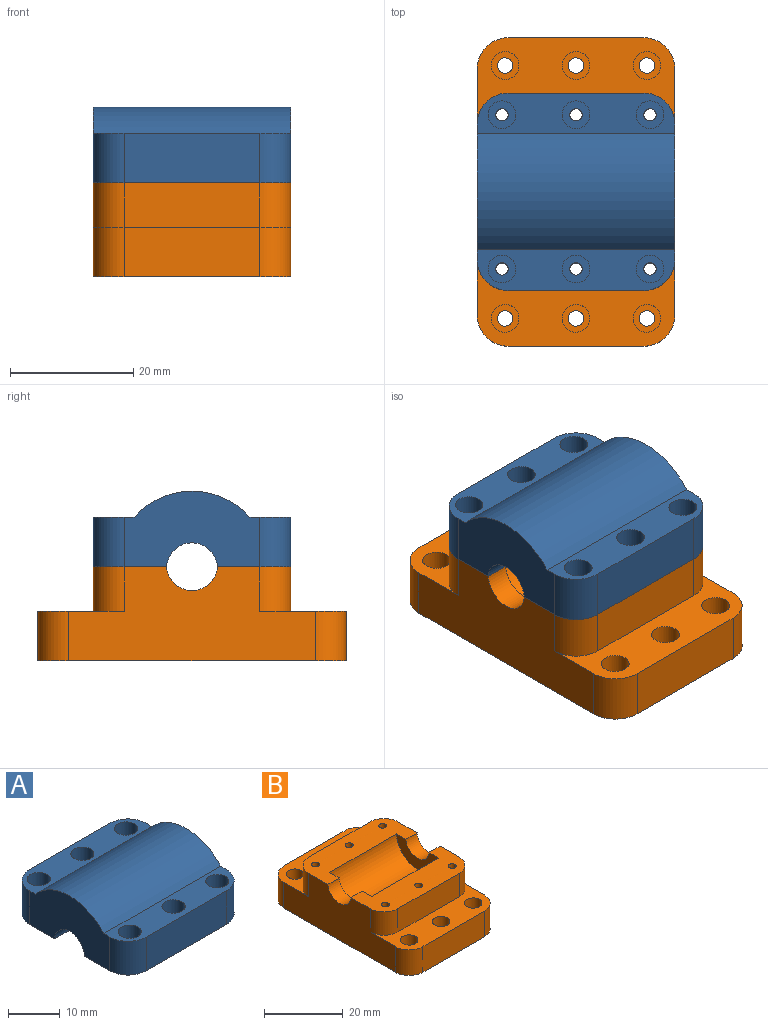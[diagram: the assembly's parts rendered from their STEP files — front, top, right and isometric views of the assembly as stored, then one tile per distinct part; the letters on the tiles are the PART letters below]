
ASSEMBLY  parts=2 mates=1
PART A: 81 faces, bbox 32x32x12.2 mm
  f0: plane 22x12.25mm, normal (1,0,0), area 191mm2, adj f8,f10,f11,f12,f14,f15,f22,f23
  f1: cylinder r=1mm len=4mm, axis (0,0,-1), area 25.1mm2, adj f14,f35
  f2: cylinder r=1mm len=4mm, axis (0,0,-1), area 25.1mm2, adj f14,f33
  f3: cylinder r=1mm len=4mm, axis (0,0,-1), area 25.1mm2, adj f14,f31
  f4: cylinder r=1mm len=4mm, axis (0,0,-1), area 25.1mm2, adj f8,f29
  f5: cylinder r=1mm len=4mm, axis (0,0,-1), area 25.1mm2, adj f8,f27
  f6: cylinder r=1mm len=4mm, axis (0,0,-1), area 25.1mm2, adj f8,f25
  f7: cylinder r=4.12mm len=8.23mm, axis (-1,0,0), area 49.8mm2, adj f8,f14,f16,f18
  f8: plane 32x11.88mm, normal (0,0,-1), area 279mm2, adj f0,f4,f5,f6,f7,f9,f15,f16
  f9: plane 22x8mm, normal (0,1,0), area 176mm2, adj f8,f10,f20,f22
  f10: plane 32x6.61mm, normal (0,0,1), area 153.2mm2, adj f0,f9,f11,f16,f20,f22,f24,f26
  f11: cylinder r=12.5mm len=32mm, axis (-1,0,0), area 679.6mm2, adj f0,f10,f12,f16
  f12: plane 32x6.61mm, normal (0,0,1), area 153.2mm2, adj f0,f11,f13,f16,f21,f23,f30,f32
  f13: plane 22x8mm, normal (0,-1,0), area 176mm2, adj f12,f14,f21,f23
  f14: plane 32x11.88mm, normal (0,0,-1), area 279mm2, adj f0,f1,f2,f3,f7,f13,f15,f16
  f15: cylinder r=4.12mm len=8.23mm, axis (-1,0,0), area 49.8mm2, adj f0,f8,f14,f19
  f16: plane 22x12.25mm, normal (-1,0,0), area 206.6mm2, adj f7,f8,f10,f11,f12,f14,f20,f21
  f17: cylinder r=7.5mm len=24mm, axis (1,0,0), area 553.3mm2, adj f8,f14,f18,f19
  f18: plane 14.99x7.25mm, normal (1,0,0), area 59.9mm2, adj f7,f8,f14,f17
  f19: plane 14.99x7.25mm, normal (-1,0,0), area 59.9mm2, adj f8,f14,f15,f17
  f20: cylinder r=5mm len=8mm, axis (0,0,1), area 62.8mm2, adj f8,f9,f10,f16
  f21: cylinder r=5mm len=8mm, axis (0,0,-1), area 62.8mm2, adj f12,f13,f14,f16
  f22: cylinder r=5mm len=8mm, axis (0,0,-1), area 62.8mm2, adj f0,f8,f9,f10
  f23: cylinder r=5mm len=8mm, axis (0,0,1), area 62.8mm2, adj f0,f12,f13,f14
  f24: cylinder r=2.25mm len=4.5mm, axis (0,0,1), area 56.5mm2, adj f10,f25
  f25: plane 4.5x4.5mm, normal (0,0,1), area 12.8mm2, adj f6,f24
  f26: cylinder r=2.25mm len=4.5mm, axis (0,0,1), area 56.5mm2, adj f10,f27
  f27: plane 4.5x4.5mm, normal (0,0,1), area 12.8mm2, adj f5,f26
  f28: cylinder r=2.25mm len=4.5mm, axis (0,0,1), area 56.5mm2, adj f10,f29
  f29: plane 4.5x4.5mm, normal (0,0,1), area 12.8mm2, adj f4,f28
  f30: cylinder r=2.25mm len=4.5mm, axis (0,0,1), area 56.5mm2, adj f12,f31
  f31: plane 4.5x4.5mm, normal (0,0,1), area 12.8mm2, adj f3,f30
  f32: cylinder r=2.25mm len=4.5mm, axis (0,0,1), area 56.5mm2, adj f12,f33
  f33: plane 4.5x4.5mm, normal (0,0,1), area 12.8mm2, adj f2,f32
  f34: cylinder r=2.25mm len=4.5mm, axis (0,0,1), area 56.5mm2, adj f12,f35
  f35: plane 4.5x4.5mm, normal (0,0,1), area 12.8mm2, adj f1,f34
  f36: plane 1.5x1.04mm, normal (0,0,-1), area 1.6mm2, adj f0,f37,f39,f40
  f37: plane 6.41x1.5mm, normal (0,1,0), area 9.6mm2, adj f0,f36,f38,f40
  f38: plane 1.5x1.04mm, normal (0,0,1), area 1.6mm2, adj f0,f37,f39,f40
  f39: plane 6.41x1.5mm, normal (0,-1,0), area 9.6mm2, adj f0,f36,f38,f40
  f40: plane 6.41x1.04mm, normal (1,0,0), area 6.7mm2, adj f36,f37,f38,f39
  f41: extruded ~1.5x0.43mm, area 0.7mm2, adj f0,f42,f79,f80
  f42: extruded ~1.5x0.33mm, area 0.5mm2, adj f0,f41,f43,f80
  f43: extruded ~1.5x0.3mm, area 0.6mm2, adj f0,f42,f44,f80
  f44: extruded ~1.5x0.39mm, area 0.7mm2, adj f0,f43,f45,f80
  f45: extruded ~1.5x0.49mm, area 0.8mm2, adj f0,f44,f46,f80
  f46: extruded ~1.5x0.8mm, area 1.2mm2, adj f0,f45,f47,f80
  f47: extruded ~1.5x0.54mm, area 1.1mm2, adj f0,f46,f48,f80
  f48: extruded ~1.5x0.68mm, area 1.1mm2, adj f0,f47,f49,f80
  f49: extruded ~1.5x0.79mm, area 1.2mm2, adj f0,f48,f50,f80
  f50: plane 1.5x0.44mm, normal (0,0,-1), area 0.7mm2, adj f0,f49,f51,f80
  f51: plane 1.5x0.79mm, normal (0,1,0), area 1.2mm2, adj f0,f50,f52,f80
  f52: plane 1.5x0.34mm, normal (0,0,1), area 0.5mm2, adj f0,f51,f53,f80
  f53: extruded ~1.5x0.64mm, area 1mm2, adj f0,f52,f54,f80
  f54: extruded ~1.5x0.37mm, area 0.7mm2, adj f0,f53,f55,f80
  f55: extruded ~1.5x0.31mm, area 0.5mm2, adj f0,f54,f56,f80
  f56: extruded ~1.5x0.33mm, area 0.5mm2, adj f0,f55,f57,f80
  f57: extruded ~1.5x0.6mm, area 0.9mm2, adj f0,f56,f58,f80
  f58: extruded ~1.5x0.3mm, area 0.6mm2, adj f0,f57,f59,f80
  f59: extruded ~1.5x0.37mm, area 0.6mm2, adj f0,f58,f60,f80
  f60: extruded ~1.5x0.39mm, area 0.6mm2, adj f0,f59,f61,f80
  f61: plane 1.5x0.42mm, normal (0,0,-1), area 0.6mm2, adj f0,f60,f62,f80
  f62: plane 1.5x0.71mm, normal (0,1,0), area 1.1mm2, adj f0,f61,f63,f80
  f63: plane 1.5x0.87mm, normal (0,0,1), area 1.3mm2, adj f0,f62,f64,f80
  f64: extruded ~1.5x0.79mm, area 1.3mm2, adj f0,f63,f65,f80
  f65: extruded ~1.5x0.79mm, area 1.3mm2, adj f0,f64,f66,f80
  f66: extruded ~1.5x0.79mm, area 1.3mm2, adj f0,f65,f67,f80
  f67: extruded ~1.5x0.72mm, area 1.2mm2, adj f0,f66,f68,f80
  f68: plane 1.5x0.95mm, normal (0,0,-1), area 1.4mm2, adj f0,f67,f69,f80
  f69: plane 1.5x0.77mm, normal (0,1,0), area 1.1mm2, adj f0,f68,f70,f80
  f70: plane 1.5x1.01mm, normal (0,0,1), area 1.5mm2, adj f0,f69,f71,f80
  f71: extruded ~1.5x0.22mm, area 0.3mm2, adj f0,f70,f72,f80
  f72: extruded ~1.5x0.38mm, area 0.6mm2, adj f0,f71,f73,f80
  f73: extruded ~1.5x0.44mm, area 0.7mm2, adj f0,f72,f74,f80
  f74: extruded ~1.5x0.43mm, area 0.8mm2, adj f0,f73,f75,f80
  f75: extruded ~1.5x0.52mm, area 0.9mm2, adj f0,f74,f76,f80
  f76: extruded ~1.5x0.75mm, area 1.1mm2, adj f0,f75,f77,f80
  f77: extruded ~1.5x0.63mm, area 1mm2, adj f0,f76,f78,f80
  f78: extruded ~1.5x0.47mm, area 0.9mm2, adj f0,f77,f79,f80
  f79: extruded ~1.5x0.42mm, area 0.8mm2, adj f0,f41,f78,f80
  f80: plane 6.41x2.93mm, normal (1,0,0), area 8.9mm2, adj f41,f42,f43,f44,f45,f46,f47,f48
PART B: 48 faces, bbox 32x50x15.3 mm
  f0: cylinder r=1.25mm len=4mm, axis (0,0,1), area 31.4mm2, adj f16,f39
  f1: cylinder r=1.25mm len=4mm, axis (0,0,1), area 31.4mm2, adj f16,f41
  f2: cylinder r=1.25mm len=4mm, axis (0,0,1), area 31.4mm2, adj f16,f35
  f3: cylinder r=1.25mm len=4mm, axis (0,0,1), area 31.4mm2, adj f16,f33
  f4: cylinder r=1.25mm len=4mm, axis (0,0,1), area 31.4mm2, adj f16,f37
  f5: cylinder r=1.25mm len=4mm, axis (0,0,1), area 31.4mm2, adj f16,f43
  f6: plane 32.01x11.89mm, normal (0,0,1), area 279.1mm2, adj f8,f9,f14,f18,f19,f20,f21,f23
  f7: plane 32.01x11.89mm, normal (0,0,1), area 278.9mm2, adj f8,f9,f14,f18,f19,f20,f21,f22
  f8: plane 40x15.25mm, normal (1,0,0), area 454.8mm2, adj f6,f7,f12,f13,f16,f18,f29,f31
  f9: plane 40x15.25mm, normal (-1,0,0), area 454.8mm2, adj f6,f7,f10,f11,f14,f16,f29,f31
  f10: cylinder r=5mm len=8mm, axis (0,0,1), area 62.8mm2, adj f9,f16,f17,f31
  f11: cylinder r=5mm len=8mm, axis (0,0,-1), area 62.8mm2, adj f9,f15,f16,f29
  f12: cylinder r=5mm len=8mm, axis (0,0,-1), area 62.8mm2, adj f8,f16,f17,f31
  f13: cylinder r=5mm len=8mm, axis (0,0,1), area 62.8mm2, adj f8,f15,f16,f29
  f14: cylinder r=4.12mm len=8.23mm, axis (-1,0,0), area 49.8mm2, adj f6,f7,f9,f20
  f15: plane 22x8mm, normal (0,-1,0), area 176mm2, adj f11,f13,f16,f29
  f16: plane 50x32mm, normal (0,0,-1), area 1530.2mm2, adj f0,f1,f2,f3,f4,f5,f8,f9
  f17: plane 22x8mm, normal (0,1,0), area 176mm2, adj f10,f12,f16,f31
  f18: cylinder r=4.12mm len=8.23mm, axis (-1,0,0), area 49.8mm2, adj f6,f7,f8,f21
  f19: cylinder r=7.5mm len=24mm, axis (1,0,0), area 553.3mm2, adj f6,f7,f20,f21
  f20: plane 14.99x7.25mm, normal (1,0,0), area 59.9mm2, adj f6,f7,f14,f19
  f21: plane 14.99x7.25mm, normal (-1,0,0), area 59.9mm2, adj f6,f7,f18,f19
  f22: cylinder r=1mm len=15.25mm, axis (0,0,1), area 95.8mm2, adj f7,f16
  f23: cylinder r=1mm len=15.25mm, axis (0,0,1), area 95.8mm2, adj f6,f16
  f24: cylinder r=1mm len=15.25mm, axis (0,0,1), area 95.8mm2, adj f6,f16
  f25: cylinder r=1mm len=15.25mm, axis (0,0,1), area 95.8mm2, adj f6,f16
  f26: cylinder r=1mm len=15.25mm, axis (0,0,1), area 95.8mm2, adj f7,f16
  f27: cylinder r=1mm len=15.25mm, axis (0,0,1), area 95.8mm2, adj f7,f16
  f28: plane 22x7.25mm, normal (0,-1,0), area 159.4mm2, adj f7,f29,f44,f45
  f29: plane 32x14mm, normal (0,0,1), area 240.3mm2, adj f8,f9,f11,f13,f15,f28,f38,f40
  f30: plane 22x7.25mm, normal (0,1,0), area 159.4mm2, adj f6,f31,f46,f47
  f31: plane 32x14mm, normal (0,0,1), area 240.3mm2, adj f8,f9,f10,f12,f17,f30,f32,f34
  f32: cylinder r=2.25mm len=4.5mm, axis (0,0,1), area 56.5mm2, adj f31,f33
  f33: plane 4.5x4.5mm, normal (0,0,1), area 11mm2, adj f3,f32
  f34: cylinder r=2.25mm len=4.5mm, axis (0,0,1), area 56.5mm2, adj f31,f35
  f35: plane 4.5x4.5mm, normal (0,0,1), area 11mm2, adj f2,f34
  f36: cylinder r=2.25mm len=4.5mm, axis (0,0,1), area 56.5mm2, adj f31,f37
  f37: plane 4.5x4.5mm, normal (0,0,1), area 11mm2, adj f4,f36
  f38: cylinder r=2.25mm len=4.5mm, axis (0,0,1), area 56.5mm2, adj f29,f39
  f39: plane 4.5x4.5mm, normal (0,0,1), area 11mm2, adj f0,f38
  f40: cylinder r=2.25mm len=4.5mm, axis (0,0,1), area 56.5mm2, adj f29,f41
  f41: plane 4.5x4.5mm, normal (0,0,1), area 11mm2, adj f1,f40
  f42: cylinder r=2.25mm len=4.5mm, axis (0,0,1), area 56.5mm2, adj f29,f43
  f43: plane 4.5x4.5mm, normal (0,0,1), area 11mm2, adj f5,f42
  f44: cylinder r=5mm len=7.25mm, axis (0,0,1), area 56.9mm2, adj f7,f8,f28,f29
  f45: cylinder r=5mm len=7.25mm, axis (0,0,-1), area 56.9mm2, adj f7,f9,f28,f29
  f46: cylinder r=5mm len=7.25mm, axis (0,0,1), area 56.9mm2, adj f6,f9,f30,f31
  f47: cylinder r=5mm len=7.25mm, axis (0,0,-1), area 56.9mm2, adj f6,f8,f30,f31
PLACE A t=(0.19,-0.05,7.34)mm
PLACE B t=(-15.81,-0.05,-7.66)mm
MATE planar A.f3 <-> B.f22  axis (0,0,-1) through (-11.81,-12.55,7.59)mm
